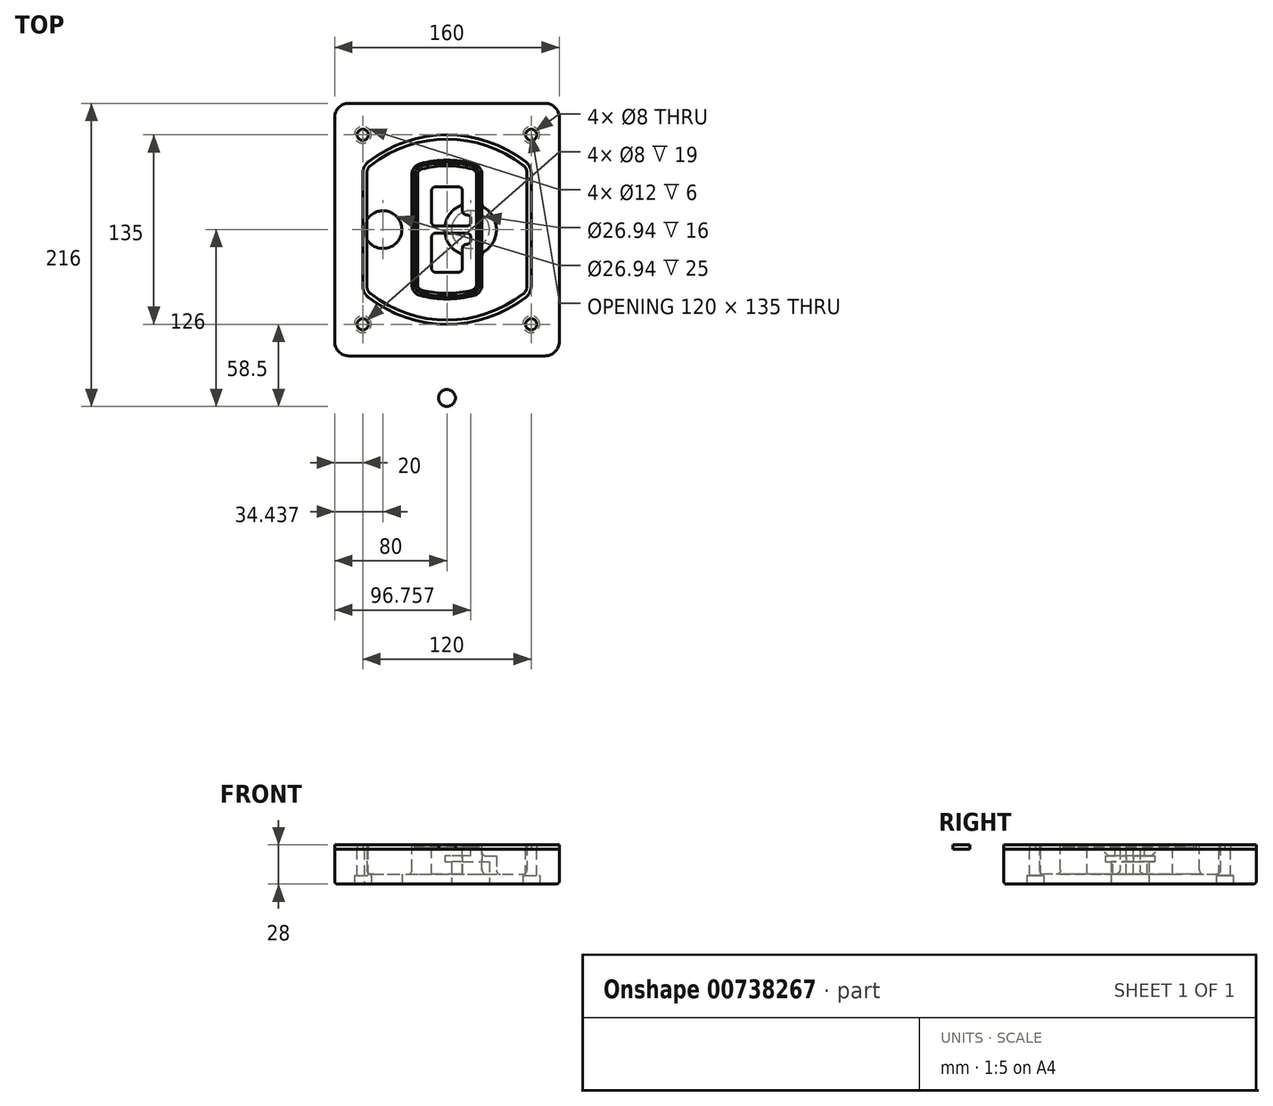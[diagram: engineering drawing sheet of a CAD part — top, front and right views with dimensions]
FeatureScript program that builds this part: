
annotation { "Feature Type Name" : "Feature", "Feature Type Description" : "" }
export const myFeature = defineFeature(function(context is Context, id is Id, definition is map)
    precondition{}
    {
        {
            var Q0;
            Q0=qCreatedBy(makeId("Top.planeOp"),FACE);
            var sketch = newSketch(context, id + "F0", { "sketchPlane" : qUnion([Q0])});
            skPoint(sketch, "E0.rect.middle", {"position": v(0, 0) * mm});
            skLineSegment(sketch, "E1.bottom", {"start": v(-70, -90) * mm, "end": v(70, -90) * mm});
            skLineSegment(sketch, "E1.top", {"start": v(-70, 90) * mm, "end": v(70, 90) * mm});
            skLineSegment(sketch, "E1.left", {"start": v(-80, -80) * mm, "end": v(-80, 80) * mm});
            skLineSegment(sketch, "E1.right", {"start": v(80, -80) * mm, "end": v(80, 80) * mm});
            skLineSegment(sketch, "E2", {"start": v(-80, 90) * mm, "end": v(80, -90) * mm, "construction": true});
            skLineSegment(sketch, "E3", {"start": v(80, 90) * mm, "end": v(-80, -90) * mm, "construction": true});
            skCircle(sketch, "E4", {"center": v(-60, 67.5) * mm, "radius": 4 * mm});
            skCircle(sketch, "E5", {"center": v(60, 67.5) * mm, "radius": 4 * mm});
            skCircle(sketch, "E6", {"center": v(60, -67.5) * mm, "radius": 4 * mm});
            skCircle(sketch, "E7", {"center": v(-60, -67.5) * mm, "radius": 4 * mm});
            skLineSegment(sketch, "E8", {"start": v(-60, 67.5) * mm, "end": v(60, 67.5) * mm, "construction": true});
            skLineSegment(sketch, "E9", {"start": v(60, 67.5) * mm, "end": v(60, -67.5) * mm, "construction": true});
            skLineSegment(sketch, "E10", {"start": v(60, -67.5) * mm, "end": v(-60, -67.5) * mm, "construction": true});
            skLineSegment(sketch, "E11", {"start": v(-60, -67.5) * mm, "end": v(-60, 67.5) * mm, "construction": true});
            skLineSegment(sketch, "E12", {"start": v(-60, 40.3) * mm, "end": v(-60, -40.3) * mm});
            skLineSegment(sketch, "E13", {"start": v(60, 40.3) * mm, "end": v(60, -40.3) * mm});
            skArc(sketch, "E14", {"start": v(56.15, 48.18) * mm, "mid": v(0, 67.5) * mm, "end": v(-56.15, 48.18) * mm});
            skArc(sketch, "E15", {"start": v(-56.15, -48.18) * mm, "mid": v(0, -67.5) * mm, "end": v(56.15, -48.18) * mm});
            skLineSegment(sketch, "E16", {"start": v(-60, 0) * mm, "end": v(60, 0) * mm, "construction": true});
            skPoint(sketch, "E17.visualSharp", {"position": v(-60, -45) * mm});
            skArc(sketch, "E17.filletArc", {"start": v(-60, -40.3) * mm, "mid": v(-58.99, -44.68) * mm, "end": v(-56.15, -48.18) * mm});
            skPoint(sketch, "E18.visualSharp", {"position": v(-60, 45) * mm});
            skArc(sketch, "E18.filletArc", {"start": v(-56.15, 48.18) * mm, "mid": v(-58.99, 44.68) * mm, "end": v(-60, 40.3) * mm});
            skPoint(sketch, "E19.visualSharp", {"position": v(60, 45) * mm});
            skArc(sketch, "E19.filletArc", {"start": v(60, 40.3) * mm, "mid": v(58.99, 44.68) * mm, "end": v(56.15, 48.18) * mm});
            skPoint(sketch, "E20.visualSharp", {"position": v(60, -45) * mm});
            skArc(sketch, "E20.filletArc", {"start": v(56.15, -48.18) * mm, "mid": v(58.99, -44.68) * mm, "end": v(60, -40.3) * mm});
            skPoint(sketch, "E21.visualSharp", {"position": v(-80, 90) * mm});
            skArc(sketch, "E21.filletArc", {"start": v(-70, 90) * mm, "mid": v(-77.07, 87.07) * mm, "end": v(-80, 80) * mm});
            skPoint(sketch, "E22.visualSharp", {"position": v(80, 90) * mm});
            skArc(sketch, "E22.filletArc", {"start": v(80, 80) * mm, "mid": v(77.07, 87.07) * mm, "end": v(70, 90) * mm});
            skPoint(sketch, "E23.visualSharp", {"position": v(80, -90) * mm});
            skArc(sketch, "E23.filletArc", {"start": v(70, -90) * mm, "mid": v(77.07, -87.07) * mm, "end": v(80, -80) * mm});
            skPoint(sketch, "E24.visualSharp", {"position": v(-80, -90) * mm});
            skArc(sketch, "E24.filletArc", {"start": v(-80, -80) * mm, "mid": v(-77.07, -87.07) * mm, "end": v(-70, -90) * mm});
            skArc(sketch, "E25.0", {"start": v(57, 40.3) * mm, "mid": v(56.3, 43.36) * mm, "end": v(54.3, 45.81) * mm});
            skLineSegment(sketch, "E25.1", {"start": v(57, 40.3) * mm, "end": v(57, -40.3) * mm});
            skArc(sketch, "E25.2", {"start": v(54.3, -45.81) * mm, "mid": v(56.3, -43.36) * mm, "end": v(57, -40.3) * mm});
            skArc(sketch, "E25.3", {"start": v(-54.3, -45.81) * mm, "mid": v(0, -64.5) * mm, "end": v(54.3, -45.81) * mm});
            skArc(sketch, "E25.4", {"start": v(-57, -40.3) * mm, "mid": v(-56.3, -43.36) * mm, "end": v(-54.3, -45.81) * mm});
            skArc(sketch, "E25.5", {"start": v(54.3, 45.81) * mm, "mid": v(0, 64.5) * mm, "end": v(-54.3, 45.81) * mm});
            skLineSegment(sketch, "E25.6", {"start": v(-57, 40.3) * mm, "end": v(-57, -40.3) * mm});
            skArc(sketch, "E25.7", {"start": v(-54.3, 45.81) * mm, "mid": v(-56.3, 43.36) * mm, "end": v(-57, 40.3) * mm});
            skArc(sketch, "E26.0", {"start": v(-58.62, 51.33) * mm, "mid": v(-62.58, 46.43) * mm, "end": v(-64, 40.3) * mm});
            skArc(sketch, "E26.1", {"start": v(58.62, 51.33) * mm, "mid": v(0, 71.5) * mm, "end": v(-58.62, 51.33) * mm});
            skArc(sketch, "E26.2", {"start": v(64, 40.3) * mm, "mid": v(62.58, 46.43) * mm, "end": v(58.62, 51.33) * mm});
            skLineSegment(sketch, "E26.3", {"start": v(64, 40.3) * mm, "end": v(64, -40.3) * mm});
            skArc(sketch, "E26.4", {"start": v(58.62, -51.33) * mm, "mid": v(62.58, -46.43) * mm, "end": v(64, -40.3) * mm});
            skLineSegment(sketch, "E26.5", {"start": v(-64, 40.3) * mm, "end": v(-64, -40.3) * mm});
            skArc(sketch, "E26.6", {"start": v(-58.62, -51.33) * mm, "mid": v(0, -71.5) * mm, "end": v(58.62, -51.33) * mm});
            skArc(sketch, "E26.7", {"start": v(-64, -40.3) * mm, "mid": v(-62.58, -46.43) * mm, "end": v(-58.62, -51.33) * mm});
            skSolve(sketch);
        }
        {
            var Q0;
            Q0=makeQuery(id+"F0.imprint","IMPRINT",FACE,{"disambiguationData":[TD([[makeQuery(id+"F0.imprint","IMPRINT",EDGE,{"derivedFrom":sQuery(id+"F0.wireOp",EDGE,"E1.bottom")}),1.0]])]});
            var Q1;
            Q1=makeQuery(id+"F0.imprint","IMPRINT",FACE,{"disambiguationData":[TD([[makeQuery(id+"F0.imprint","IMPRINT",EDGE,{"derivedFrom":sQuery(id+"F0.wireOp",EDGE,"E12")}),1.0]])]});
            var Q2;
            Q2=makeQuery(id+"F0.imprint","IMPRINT",FACE,{"disambiguationData":[TD([[makeQuery(id+"F0.imprint","IMPRINT",EDGE,{"derivedFrom":sQuery(id+"F0.wireOp",EDGE,"E25.0")}),1.0]])]});
            var Q3;
            Q3=makeQuery(id+"F0.imprint","IMPRINT",FACE,{"disambiguationData":[TD([[makeQuery(id+"F0.imprint","IMPRINT",EDGE,{"derivedFrom":sQuery(id+"F0.wireOp",EDGE,"E12")}),-1.0]])]});
            extrude(context, id + "F1", {"entities" : qUnion([Q0, Q1, Q2, Q3]), "oppositeDirection" : true, "depth" : 25 * mm});
        }
        {
            var Q0;
            Q0=makeQuery(id+"F0.imprint","IMPRINT",FACE,{"disambiguationData":[TD([[makeQuery(id+"F0.imprint","IMPRINT",EDGE,{"derivedFrom":sQuery(id+"F0.wireOp",EDGE,"E12")}),1.0]])]});
            extrude(context, id + "F2", {"entities" : qUnion([Q0]), "operationType" : NewBodyOperationType.ADD, "depth" : 3 * mm});
        }
        {
            var Q0;
            Q0=makeQuery(id+"F0.imprint","IMPRINT",FACE,{"disambiguationData":[TD([[makeQuery(id+"F0.imprint","IMPRINT",EDGE,{"derivedFrom":sQuery(id+"F0.wireOp",EDGE,"E25.0")}),1.0]])]});
            extrude(context, id + "F3", {"entities" : qUnion([Q0]), "operationType" : NewBodyOperationType.REMOVE, "oppositeDirection" : true, "depth" : 18 * mm});
        }
        {
            var Q0;
            Q0=makeQuery(id+"F2.opExtrude","CAP_FACE",FACE,{"disambiguationData":[OSD([sQuery(id+"F0.wireOp",EDGE,"E12"),sQuery(id+"F0.wireOp",EDGE,"E13"),sQuery(id+"F0.wireOp",EDGE,"E14"),sQuery(id+"F0.wireOp",EDGE,"E15"),sQuery(id+"F0.wireOp",EDGE,"E17.filletArc"),sQuery(id+"F0.wireOp",EDGE,"E18.filletArc"),sQuery(id+"F0.wireOp",EDGE,"E19.filletArc"),sQuery(id+"F0.wireOp",EDGE,"E20.filletArc"),sQuery(id+"F0.wireOp",EDGE,"E25.0"),sQuery(id+"F0.wireOp",EDGE,"E25.1"),sQuery(id+"F0.wireOp",EDGE,"E25.2"),sQuery(id+"F0.wireOp",EDGE,"E25.3"),sQuery(id+"F0.wireOp",EDGE,"E25.4"),sQuery(id+"F0.wireOp",EDGE,"E25.5"),sQuery(id+"F0.wireOp",EDGE,"E25.6"),sQuery(id+"F0.wireOp",EDGE,"E25.7")])],"isStart":false});
            var sketch = newSketch(context, id + "F4", { "sketchPlane" : qUnion([Q0])});
            skArc(sketch, "E27.0", {"start": v(-19.08, -46.97) * mm, "mid": v(0, -49.5) * mm, "end": v(19.08, -46.97) * mm});
            skArc(sketch, "E28.0", {"start": v(19.08, 46.97) * mm, "mid": v(0, 49.5) * mm, "end": v(-19.08, 46.97) * mm});
            skLineSegment(sketch, "E29", {"start": v(-25, 39.25) * mm, "end": v(-25, -39.25) * mm});
            skLineSegment(sketch, "E30", {"start": v(25, 39.25) * mm, "end": v(25, -39.25) * mm});
            skLineSegment(sketch, "E31", {"start": v(-25, 45.1) * mm, "end": v(25, 45.1) * mm, "construction": true});
            skLineSegment(sketch, "E32", {"start": v(-25, -45.1) * mm, "end": v(25, -45.1) * mm, "construction": true});
            skPoint(sketch, "E33.visualSharp", {"position": v(-25, 45.1) * mm});
            skArc(sketch, "E33.filletArc", {"start": v(-19.08, 46.97) * mm, "mid": v(-23.35, 44.11) * mm, "end": v(-25, 39.25) * mm});
            skPoint(sketch, "E34.visualSharp", {"position": v(25, 45.1) * mm});
            skArc(sketch, "E34.filletArc", {"start": v(25, 39.25) * mm, "mid": v(23.35, 44.11) * mm, "end": v(19.08, 46.97) * mm});
            skPoint(sketch, "E35.visualSharp", {"position": v(25, -45.1) * mm});
            skArc(sketch, "E35.filletArc", {"start": v(19.08, -46.97) * mm, "mid": v(23.35, -44.11) * mm, "end": v(25, -39.25) * mm});
            skPoint(sketch, "E36.visualSharp", {"position": v(-25, -45.1) * mm});
            skArc(sketch, "E36.filletArc", {"start": v(-25, -39.25) * mm, "mid": v(-23.35, -44.11) * mm, "end": v(-19.08, -46.97) * mm});
            skArc(sketch, "E37.0", {"start": v(54.3, 45.81) * mm, "mid": v(0, 64.5) * mm, "end": v(-54.3, 45.81) * mm});
            skArc(sketch, "E37.1", {"start": v(-54.3, 45.81) * mm, "mid": v(-56.3, 43.36) * mm, "end": v(-57, 40.3) * mm});
            skLineSegment(sketch, "E37.2", {"start": v(-57, 40.3) * mm, "end": v(-57, -40.3) * mm});
            skArc(sketch, "E37.3", {"start": v(-57, -40.3) * mm, "mid": v(-56.3, -43.36) * mm, "end": v(-54.3, -45.81) * mm});
            skArc(sketch, "E37.4", {"start": v(-54.3, -45.81) * mm, "mid": v(0, -64.5) * mm, "end": v(54.3, -45.81) * mm});
            skArc(sketch, "E37.5", {"start": v(54.3, -45.81) * mm, "mid": v(56.3, -43.36) * mm, "end": v(57, -40.3) * mm});
            skLineSegment(sketch, "E37.6", {"start": v(57, 40.3) * mm, "end": v(57, -40.3) * mm});
            skArc(sketch, "E37.7", {"start": v(57, 40.3) * mm, "mid": v(56.3, 43.36) * mm, "end": v(54.3, 45.81) * mm});
            skLineSegment(sketch, "E38.0", {"start": v(23, 39.25) * mm, "end": v(23, -39.25) * mm});
            skArc(sketch, "E38.1", {"start": v(18.56, -45.04) * mm, "mid": v(21.76, -42.9) * mm, "end": v(23, -39.25) * mm});
            skArc(sketch, "E38.2", {"start": v(-18.56, -45.04) * mm, "mid": v(0, -47.5) * mm, "end": v(18.56, -45.04) * mm});
            skArc(sketch, "E38.3", {"start": v(-23, -39.25) * mm, "mid": v(-21.76, -42.9) * mm, "end": v(-18.56, -45.04) * mm});
            skLineSegment(sketch, "E38.4", {"start": v(-23, 39.25) * mm, "end": v(-23, -39.25) * mm});
            skArc(sketch, "E38.5", {"start": v(23, 39.25) * mm, "mid": v(21.76, 42.9) * mm, "end": v(18.56, 45.04) * mm});
            skArc(sketch, "E38.6", {"start": v(-18.56, 45.04) * mm, "mid": v(-21.76, 42.9) * mm, "end": v(-23, 39.25) * mm});
            skArc(sketch, "E38.7", {"start": v(18.56, 45.04) * mm, "mid": v(0, 47.5) * mm, "end": v(-18.56, 45.04) * mm});
            skArc(sketch, "E39.0", {"start": v(21, 39.25) * mm, "mid": v(20.18, 41.68) * mm, "end": v(18.04, 43.1) * mm});
            skLineSegment(sketch, "E39.1", {"start": v(21, 39.25) * mm, "end": v(21, -39.25) * mm});
            skArc(sketch, "E39.2", {"start": v(18.04, -43.1) * mm, "mid": v(20.18, -41.68) * mm, "end": v(21, -39.25) * mm});
            skArc(sketch, "E39.3", {"start": v(-18.04, -43.1) * mm, "mid": v(0, -45.5) * mm, "end": v(18.04, -43.1) * mm});
            skArc(sketch, "E39.4", {"start": v(-21, -39.25) * mm, "mid": v(-20.18, -41.68) * mm, "end": v(-18.04, -43.1) * mm});
            skArc(sketch, "E39.5", {"start": v(18.04, 43.1) * mm, "mid": v(0, 45.5) * mm, "end": v(-18.04, 43.1) * mm});
            skLineSegment(sketch, "E39.6", {"start": v(-21, 39.25) * mm, "end": v(-21, -39.25) * mm});
            skArc(sketch, "E39.7", {"start": v(-18.04, 43.1) * mm, "mid": v(-20.18, 41.68) * mm, "end": v(-21, 39.25) * mm});
            skLineSegment(sketch, "E40", {"start": v(-25, 0) * mm, "end": v(25, 0) * mm, "construction": true});
            skLineSegment(sketch, "E41", {"start": v(-11, 5.5) * mm, "end": v(-11, 27.5) * mm});
            skLineSegment(sketch, "E42", {"start": v(-8, 30.5) * mm, "end": v(8, 30.5) * mm});
            skLineSegment(sketch, "E43", {"start": v(11, 27.5) * mm, "end": v(11, 13.5) * mm});
            skLineSegment(sketch, "E44", {"start": v(14, 10.5) * mm, "end": v(14, 10.5) * mm});
            skLineSegment(sketch, "E45", {"start": v(17, 7.5) * mm, "end": v(17, 5.5) * mm});
            skLineSegment(sketch, "E46", {"start": v(14, 2.5) * mm, "end": v(-8, 2.5) * mm});
            skPoint(sketch, "E47.visualSharp", {"position": v(-11, 30.5) * mm});
            skArc(sketch, "E47.filletArc", {"start": v(-8, 30.5) * mm, "mid": v(-10.12, 29.62) * mm, "end": v(-11, 27.5) * mm});
            skPoint(sketch, "E48.visualSharp", {"position": v(11, 30.5) * mm});
            skArc(sketch, "E48.filletArc", {"start": v(11, 27.5) * mm, "mid": v(10.12, 29.62) * mm, "end": v(8, 30.5) * mm});
            skPoint(sketch, "E49.visualSharp", {"position": v(11, 10.5) * mm});
            skArc(sketch, "E49.filletArc", {"start": v(11, 13.5) * mm, "mid": v(11.88, 11.38) * mm, "end": v(14, 10.5) * mm});
            skPoint(sketch, "E50.visualSharp", {"position": v(17, 10.5) * mm});
            skArc(sketch, "E50.filletArc", {"start": v(17, 7.5) * mm, "mid": v(16.12, 9.62) * mm, "end": v(14, 10.5) * mm});
            skPoint(sketch, "E51.visualSharp", {"position": v(17, 2.5) * mm});
            skArc(sketch, "E51.filletArc", {"start": v(14, 2.5) * mm, "mid": v(16.12, 3.38) * mm, "end": v(17, 5.5) * mm});
            skPoint(sketch, "E52.visualSharp", {"position": v(-11, 2.5) * mm});
            skArc(sketch, "E52.filletArc", {"start": v(-11, 5.5) * mm, "mid": v(-10.12, 3.38) * mm, "end": v(-8, 2.5) * mm});
            skLineSegment(sketch, "E53.0.MirrorCS", {"start": v(14, -2.5) * mm, "end": v(-8, -2.5) * mm});
            skArc(sketch, "E54.0.MirrorCS", {"start": v(-11, -5.5) * mm, "mid": v(-10.12, -3.38) * mm, "end": v(-8, -2.5) * mm});
            skLineSegment(sketch, "E55.0.MirrorCS", {"start": v(-11, -5.5) * mm, "end": v(-11, -27.5) * mm});
            skArc(sketch, "E56.0.MirrorCS", {"start": v(-8, -30.5) * mm, "mid": v(-10.12, -29.62) * mm, "end": v(-11, -27.5) * mm});
            skLineSegment(sketch, "E57.0.MirrorCS", {"start": v(-8, -30.5) * mm, "end": v(8, -30.5) * mm});
            skArc(sketch, "E58.0.MirrorCS", {"start": v(11, -27.5) * mm, "mid": v(10.12, -29.62) * mm, "end": v(8, -30.5) * mm});
            skLineSegment(sketch, "E59.0.MirrorCS", {"start": v(11, -27.5) * mm, "end": v(11, -13.5) * mm});
            skArc(sketch, "E60.0.MirrorCS", {"start": v(11, -13.5) * mm, "mid": v(11.88, -11.38) * mm, "end": v(14, -10.5) * mm});
            skArc(sketch, "E61.0.MirrorCS", {"start": v(17, -7.5) * mm, "mid": v(16.12, -9.62) * mm, "end": v(14, -10.5) * mm});
            skLineSegment(sketch, "E62.0.MirrorCS", {"start": v(17, -7.5) * mm, "end": v(17, -5.5) * mm});
            skArc(sketch, "E63.0.MirrorCS", {"start": v(14, -2.5) * mm, "mid": v(16.12, -3.38) * mm, "end": v(17, -5.5) * mm});
            skSolve(sketch);
        }
        {
            var Q0;
            Q0=makeQuery(id+"F4.imprint","IMPRINT",FACE,{"disambiguationData":[TD([[makeQuery(id+"F4.imprint","IMPRINT",EDGE,{"derivedFrom":sQuery(id+"F4.wireOp",EDGE,"E27.0")}),1.0]])]});
            var Q1;
            Q1=makeQuery(id+"F4.imprint","IMPRINT",FACE,{"disambiguationData":[TD([[makeQuery(id+"F4.imprint","IMPRINT",EDGE,{"derivedFrom":sQuery(id+"F4.wireOp",EDGE,"E38.0")}),-1.0]])]});
            var Q2;
            Q2=makeQuery(id+"F4.imprint","IMPRINT",FACE,{"disambiguationData":[TD([[makeQuery(id+"F4.imprint","IMPRINT",EDGE,{"derivedFrom":sQuery(id+"F4.wireOp",EDGE,"E39.0")}),1.0]])]});
            extrude(context, id + "F5", {"entities" : qUnion([Q0, Q1, Q2]), "operationType" : NewBodyOperationType.ADD, "endBound" : BoundingType.UP_TO_NEXT, "oppositeDirection" : true, "depth" : 25 * mm});
        }
        {
            var Q0;
            Q0=makeQuery(id+"F4.imprint","IMPRINT",FACE,{"disambiguationData":[TD([[makeQuery(id+"F4.imprint","IMPRINT",EDGE,{"derivedFrom":sQuery(id+"F4.wireOp",EDGE,"E38.0")}),-1.0]])]});
            extrude(context, id + "F6", {"entities" : qUnion([Q0]), "operationType" : NewBodyOperationType.REMOVE, "oppositeDirection" : true, "depth" : 2 * mm});
        }
        {
            var Q0;
            Q0=makeQuery(id+"F1.opExtrude","CAP_FACE",FACE,{"disambiguationData":[OSD([sQuery(id+"F0.wireOp",EDGE,"E1.bottom"),sQuery(id+"F0.wireOp",EDGE,"E1.top"),sQuery(id+"F0.wireOp",EDGE,"E1.left"),sQuery(id+"F0.wireOp",EDGE,"E1.right"),sQuery(id+"F0.wireOp",EDGE,"E4"),sQuery(id+"F0.wireOp",EDGE,"E5"),sQuery(id+"F0.wireOp",EDGE,"E6"),sQuery(id+"F0.wireOp",EDGE,"E7"),sQuery(id+"F0.wireOp",EDGE,"E21.filletArc"),sQuery(id+"F0.wireOp",EDGE,"E22.filletArc"),sQuery(id+"F0.wireOp",EDGE,"E23.filletArc"),sQuery(id+"F0.wireOp",EDGE,"E24.filletArc")])],"isStart":false});
            var sketch = newSketch(context, id + "F7", { "sketchPlane" : qUnion([Q0])});
            skCircle(sketch, "E64", {"center": v(16.76, 0) * mm, "radius": 13.47 * mm});
            skCircle(sketch, "E65", {"center": v(-45.56, 0) * mm, "radius": 13.47 * mm});
            skLineSegment(sketch, "E66", {"start": v(80, 0) * mm, "end": v(-80, 0) * mm});
            skCircle(sketch, "E67", {"center": v(16.76, 0) * mm, "radius": 18.47 * mm});
            skCircle(sketch, "E68", {"center": v(60, -67.5) * mm, "radius": 6 * mm});
            skCircle(sketch, "E69", {"center": v(-60, -67.5) * mm, "radius": 6 * mm});
            skCircle(sketch, "E70", {"center": v(-60, 67.5) * mm, "radius": 6 * mm});
            skCircle(sketch, "E71", {"center": v(60, 67.5) * mm, "radius": 6 * mm});
            skSolve(sketch);
        }
        {
            var Q0;
            {var subQ1=sQuery(id+"F7.wireOp",EDGE,"E66");var subQ4=sQuery(id+"F7.wireOp",EDGE,"E64");var subQ6=makeQuery(id+"F7.imprint","INTERSECT",VERTEX,{"disambiguationData":[OD(0.0)],"derivedFrom":[subQ4,subQ1]});Q0=makeQuery(id+"F7.imprint","IMPRINT",FACE,{"disambiguationData":[TD([[makeQuery(id+"F7.imprint","IMPRINT",EDGE,{"disambiguationData":[TD([[subQ6,-1.0]])],"derivedFrom":subQ4}),-1.0]])]});}
            var Q1;
            {var subQ0=sQuery(id+"F7.wireOp",EDGE,"E66");var subQ1=sQuery(id+"F7.wireOp",EDGE,"E64");var subQ3=makeQuery(id+"F7.imprint","INTERSECT",VERTEX,{"disambiguationData":[OD(0.0)],"derivedFrom":[subQ1,subQ0]});Q1=makeQuery(id+"F7.imprint","IMPRINT",FACE,{"disambiguationData":[TD([[makeQuery(id+"F7.imprint","IMPRINT",EDGE,{"disambiguationData":[TD([[subQ3,-1.0]])],"derivedFrom":subQ1}),1.0]])]});}
            var Q2;
            {var subQ0=sQuery(id+"F7.wireOp",EDGE,"E66");var subQ1=sQuery(id+"F7.wireOp",EDGE,"E64");var subQ3=makeQuery(id+"F7.imprint","INTERSECT",VERTEX,{"disambiguationData":[OD(0.0)],"derivedFrom":[subQ1,subQ0]});Q2=makeQuery(id+"F7.imprint","IMPRINT",FACE,{"disambiguationData":[TD([[makeQuery(id+"F7.imprint","IMPRINT",EDGE,{"disambiguationData":[TD([[subQ3,1.0]])],"derivedFrom":subQ1}),1.0]])]});}
            var Q3;
            {var subQ1=sQuery(id+"F7.wireOp",EDGE,"E66");var subQ4=sQuery(id+"F7.wireOp",EDGE,"E64");var subQ6=makeQuery(id+"F7.imprint","INTERSECT",VERTEX,{"disambiguationData":[OD(0.0)],"derivedFrom":[subQ4,subQ1]});Q3=makeQuery(id+"F7.imprint","IMPRINT",FACE,{"disambiguationData":[TD([[makeQuery(id+"F7.imprint","IMPRINT",EDGE,{"disambiguationData":[TD([[subQ6,1.0]])],"derivedFrom":subQ4}),-1.0]])]});}
            extrude(context, id + "F8", {"entities" : qUnion([Q0, Q1, Q2, Q3]), "operationType" : NewBodyOperationType.ADD, "oppositeDirection" : true, "depth" : 20 * mm});
        }
        {
            var Q0;
            {var subQ0=sQuery(id+"F7.wireOp",EDGE,"E66");var subQ1=sQuery(id+"F7.wireOp",EDGE,"E64");var subQ3=makeQuery(id+"F7.imprint","INTERSECT",VERTEX,{"disambiguationData":[OD(0.0)],"derivedFrom":[subQ1,subQ0]});Q0=makeQuery(id+"F7.imprint","IMPRINT",FACE,{"disambiguationData":[TD([[makeQuery(id+"F7.imprint","IMPRINT",EDGE,{"disambiguationData":[TD([[subQ3,-1.0]])],"derivedFrom":subQ1}),1.0]])]});}
            var Q1;
            {var subQ0=sQuery(id+"F7.wireOp",EDGE,"E66");var subQ1=sQuery(id+"F7.wireOp",EDGE,"E64");var subQ3=makeQuery(id+"F7.imprint","INTERSECT",VERTEX,{"disambiguationData":[OD(0.0)],"derivedFrom":[subQ1,subQ0]});Q1=makeQuery(id+"F7.imprint","IMPRINT",FACE,{"disambiguationData":[TD([[makeQuery(id+"F7.imprint","IMPRINT",EDGE,{"disambiguationData":[TD([[subQ3,1.0]])],"derivedFrom":subQ1}),1.0]])]});}
            extrude(context, id + "F9", {"entities" : qUnion([Q0, Q1]), "operationType" : NewBodyOperationType.REMOVE, "oppositeDirection" : true, "depth" : 16 * mm});
        }
        {
            var Q0;
            {var subQ0=sQuery(id+"F7.wireOp",EDGE,"E66");var subQ1=sQuery(id+"F7.wireOp",EDGE,"E65");var subQ3=makeQuery(id+"F7.imprint","INTERSECT",VERTEX,{"disambiguationData":[OD(0.0)],"derivedFrom":[subQ1,subQ0]});Q0=makeQuery(id+"F7.imprint","IMPRINT",FACE,{"disambiguationData":[TD([[makeQuery(id+"F7.imprint","IMPRINT",EDGE,{"disambiguationData":[TD([[subQ3,-1.0]])],"derivedFrom":subQ1}),1.0]])]});}
            var Q1;
            {var subQ0=sQuery(id+"F7.wireOp",EDGE,"E66");var subQ1=sQuery(id+"F7.wireOp",EDGE,"E65");var subQ3=makeQuery(id+"F7.imprint","INTERSECT",VERTEX,{"disambiguationData":[OD(0.0)],"derivedFrom":[subQ1,subQ0]});Q1=makeQuery(id+"F7.imprint","IMPRINT",FACE,{"disambiguationData":[TD([[makeQuery(id+"F7.imprint","IMPRINT",EDGE,{"disambiguationData":[TD([[subQ3,1.0]])],"derivedFrom":subQ1}),1.0]])]});}
            extrude(context, id + "F10", {"entities" : qUnion([Q0, Q1]), "operationType" : NewBodyOperationType.REMOVE, "oppositeDirection" : true, "depth" : 25 * mm});
        }
        {
            var Q0;
            Q0=makeQuery(id+"F7.imprint","IMPRINT",FACE,{"disambiguationData":[TD([[makeQuery(id+"F7.imprint","IMPRINT",EDGE,{"derivedFrom":sQuery(id+"F7.wireOp",EDGE,"E68")}),1.0]])]});
            var Q1;
            Q1=makeQuery(id+"F7.imprint","IMPRINT",FACE,{"disambiguationData":[TD([[makeQuery(id+"F7.imprint","IMPRINT",EDGE,{"derivedFrom":makeQuery(id+"F1.opExtrude","CAP_EDGE",EDGE,{"disambiguationData":[OSD([sQuery(id+"F0.wireOp",EDGE,"E5")])],"isStart":false})}),-1.0]])]});
            var Q2;
            Q2=makeQuery(id+"F7.imprint","IMPRINT",FACE,{"disambiguationData":[TD([[makeQuery(id+"F7.imprint","IMPRINT",EDGE,{"derivedFrom":sQuery(id+"F7.wireOp",EDGE,"E69")}),1.0]])]});
            var Q3;
            Q3=makeQuery(id+"F7.imprint","IMPRINT",FACE,{"disambiguationData":[TD([[makeQuery(id+"F7.imprint","IMPRINT",EDGE,{"derivedFrom":makeQuery(id+"F1.opExtrude","CAP_EDGE",EDGE,{"disambiguationData":[OSD([sQuery(id+"F0.wireOp",EDGE,"E4")])],"isStart":false})}),-1.0]])]});
            var Q4;
            Q4=makeQuery(id+"F7.imprint","IMPRINT",FACE,{"disambiguationData":[TD([[makeQuery(id+"F7.imprint","IMPRINT",EDGE,{"derivedFrom":sQuery(id+"F7.wireOp",EDGE,"E70")}),1.0]])]});
            var Q5;
            Q5=makeQuery(id+"F7.imprint","IMPRINT",FACE,{"disambiguationData":[TD([[makeQuery(id+"F7.imprint","IMPRINT",EDGE,{"derivedFrom":makeQuery(id+"F1.opExtrude","CAP_EDGE",EDGE,{"disambiguationData":[OSD([sQuery(id+"F0.wireOp",EDGE,"E7")])],"isStart":false})}),-1.0]])]});
            var Q6;
            Q6=makeQuery(id+"F7.imprint","IMPRINT",FACE,{"disambiguationData":[TD([[makeQuery(id+"F7.imprint","IMPRINT",EDGE,{"derivedFrom":sQuery(id+"F7.wireOp",EDGE,"E71")}),1.0]])]});
            var Q7;
            Q7=makeQuery(id+"F7.imprint","IMPRINT",FACE,{"disambiguationData":[TD([[makeQuery(id+"F7.imprint","IMPRINT",EDGE,{"derivedFrom":makeQuery(id+"F1.opExtrude","CAP_EDGE",EDGE,{"disambiguationData":[OSD([sQuery(id+"F0.wireOp",EDGE,"E6")])],"isStart":false})}),-1.0]])]});
            extrude(context, id + "F11", {"entities" : qUnion([Q0, Q1, Q2, Q3, Q4, Q5, Q6, Q7]), "operationType" : NewBodyOperationType.REMOVE, "oppositeDirection" : true, "depth" : 6 * mm});
        }
        {
            var Q0;
            Q0=makeQuery(id+"F9.boolean.opBoolean","COPY",FACE,{"derivedFrom":makeQuery(id+"F9.opExtrude","CAP_FACE",FACE,{"disambiguationData":[OSD([sQuery(id+"F7.wireOp",EDGE,"E64")])],"isStart":false})});
            var sketch = newSketch(context, id + "F12", { "sketchPlane" : qUnion([Q0])});
            skArc(sketch, "E72.0", {"start": v(11, 17.55) * mm, "mid": v(2.57, 11.82) * mm, "end": v(-1.54, 2.5) * mm});
            skArc(sketch, "E72.1", {"start": v(-1.54, -2.5) * mm, "mid": v(2.57, -11.82) * mm, "end": v(11, -17.55) * mm});
            skLineSegment(sketch, "E73", {"start": v(-1.54, -2.5) * mm, "end": v(14, -2.5) * mm});
            skLineSegment(sketch, "E74.0", {"start": v(14, 2.5) * mm, "end": v(-1.54, 2.5) * mm});
            skArc(sketch, "E74.1", {"start": v(14, 2.5) * mm, "mid": v(16.12, 3.38) * mm, "end": v(17, 5.5) * mm});
            skLineSegment(sketch, "E74.2", {"start": v(17, 7.5) * mm, "end": v(17, 5.5) * mm});
            skArc(sketch, "E74.3", {"start": v(17, 7.5) * mm, "mid": v(16.12, 9.62) * mm, "end": v(14, 10.5) * mm});
            skArc(sketch, "E74.4", {"start": v(11, 13.5) * mm, "mid": v(11.88, 11.38) * mm, "end": v(14, 10.5) * mm});
            skLineSegment(sketch, "E74.5", {"start": v(11, 17.55) * mm, "end": v(11, 13.5) * mm});
            skLineSegment(sketch, "E74.7", {"start": v(14, -2.5) * mm, "end": v(-1.54, -2.5) * mm});
            skArc(sketch, "E74.8", {"start": v(14, -2.5) * mm, "mid": v(16.12, -3.38) * mm, "end": v(17, -5.5) * mm});
            skLineSegment(sketch, "E74.9", {"start": v(17, -7.5) * mm, "end": v(17, -5.5) * mm});
            skArc(sketch, "E74.10", {"start": v(17, -7.5) * mm, "mid": v(16.12, -9.62) * mm, "end": v(14, -10.5) * mm});
            skArc(sketch, "E74.11", {"start": v(11, -13.5) * mm, "mid": v(11.88, -11.38) * mm, "end": v(14, -10.5) * mm});
            skLineSegment(sketch, "E74.12", {"start": v(11, -17.55) * mm, "end": v(11, -13.5) * mm});
            skPoint(sketch, "E75.orphan", {"position": v(11, -27.5) * mm});
            skPoint(sketch, "E76.orphan", {"position": v(-8, -2.5) * mm});
            skPoint(sketch, "E77.orphan", {"position": v(-8, 2.5) * mm});
            skPoint(sketch, "E78.orphan", {"position": v(11, 27.5) * mm});
            skSolve(sketch);
        }
        {
            var Q0;
            {var subQ7=sQuery(id+"F12.wireOp",EDGE,"E72.0");var subQ14=sQuery(id+"F12.wireOp",EDGE,"E72.1");var subQ16=sQuery(id+"F12.wireOp",EDGE,"E74.1");var subQ18=sQuery(id+"F12.wireOp",EDGE,"E74.8");Q0=qUnion([makeQuery(id+"F12.imprint","IMPRINT",FACE,{"disambiguationData":[TD([[makeQuery(id+"F12.imprint","IMPRINT",EDGE,{"derivedFrom":subQ7}),1.0]])]}),makeQuery(id+"F12.imprint","IMPRINT",FACE,{"disambiguationData":[TD([[makeQuery(id+"F12.imprint","IMPRINT",EDGE,{"derivedFrom":subQ14}),1.0]])]}),makeQuery(id+"F12.imprint","IMPRINT",FACE,{"disambiguationData":[TD([[makeQuery(id+"F12.imprint","IMPRINT",EDGE,{"derivedFrom":subQ16}),1.0]])]}),makeQuery(id+"F12.imprint","IMPRINT",FACE,{"disambiguationData":[TD([[makeQuery(id+"F12.imprint","IMPRINT",EDGE,{"derivedFrom":subQ18}),-1.0]])]})]);}
            var Q1;
            Q1=makeQuery(id+"F5.boolean.opBoolean","SPLIT",FACE,{"disambiguationData":[TD([makeQuery(id+"F5.opExtrude","SWEPT_FACE",FACE,{"disambiguationData":[OSD([sQuery(id+"F4.wireOp",EDGE,"E41")])]})])],"derivedFrom":makeQuery(id+"F3.boolean.opBoolean","COPY",FACE,{"derivedFrom":makeQuery(id+"F3.opExtrude","CAP_FACE",FACE,{"disambiguationData":[OSD([sQuery(id+"F0.wireOp",EDGE,"E25.0"),sQuery(id+"F0.wireOp",EDGE,"E25.1"),sQuery(id+"F0.wireOp",EDGE,"E25.2"),sQuery(id+"F0.wireOp",EDGE,"E25.3"),sQuery(id+"F0.wireOp",EDGE,"E25.4"),sQuery(id+"F0.wireOp",EDGE,"E25.5"),sQuery(id+"F0.wireOp",EDGE,"E25.6"),sQuery(id+"F0.wireOp",EDGE,"E25.7")])],"isStart":false})})});
            extrude(context, id + "F13", {"entities" : qUnion([Q0]), "operationType" : NewBodyOperationType.REMOVE, "endBound" : BoundingType.UP_TO_SURFACE, "endBoundEntityFace" : qUnion([Q1]), "depth" : 25 * mm});
        }
        {
            var Q0;
            Q0=makeQuery(id+"F3.boolean.opBoolean","COPY",EDGE,{"derivedFrom":makeQuery(id+"F3.opExtrude","CAP_EDGE",EDGE,{"disambiguationData":[OSD([sQuery(id+"F0.wireOp",EDGE,"E25.6")])],"isStart":false})});
            var Q1;
            Q1=makeQuery(id+"F8.boolean.opBoolean","INTERSECT",EDGE,{"derivedFrom":[makeQuery(id+"F5.opExtrude","SWEPT_FACE",FACE,{"disambiguationData":[OSD([sQuery(id+"F4.wireOp",EDGE,"E30")])]}),makeQuery(id+"F8.opExtrude","CAP_FACE",FACE,{"disambiguationData":[OSD([sQuery(id+"F7.wireOp",EDGE,"E67")])],"isStart":false})]});
            var Q2;
            Q2=makeQuery(id+"F8.boolean.opBoolean","INTERSECT",EDGE,{"disambiguationData":[OD(1.0)],"derivedFrom":[makeQuery(id+"F5.opExtrude","SWEPT_FACE",FACE,{"disambiguationData":[OSD([sQuery(id+"F4.wireOp",EDGE,"E30")])]}),makeQuery(id+"F8.opExtrude","SWEPT_FACE",FACE,{"disambiguationData":[OSD([sQuery(id+"F7.wireOp",EDGE,"E67")])]})]});
            var Q3;
            {var subQ0=sQuery(id+"F4.wireOp",EDGE,"E30");Q3=makeQuery(id+"F8.boolean.opBoolean","SPLIT",EDGE,{"disambiguationData":[TD([makeQuery(id+"F5.opExtrude","SWEPT_FACE",FACE,{"disambiguationData":[OSD([sQuery(id+"F4.wireOp",EDGE,"E35.filletArc")])]})])],"derivedFrom":makeQuery(id+"F5.opExtrude","CAP_EDGE",EDGE,{"disambiguationData":[OSD([subQ0])],"isStart":false})});}
            var Q4;
            {var subQ0=sQuery(id+"F0.wireOp",EDGE,"E25.7");var subQ1=sQuery(id+"F0.wireOp",EDGE,"E25.1");var subQ2=sQuery(id+"F0.wireOp",EDGE,"E25.6");var subQ3=sQuery(id+"F0.wireOp",EDGE,"E25.5");var subQ4=sQuery(id+"F0.wireOp",EDGE,"E25.4");var subQ5=sQuery(id+"F0.wireOp",EDGE,"E25.0");var subQ6=sQuery(id+"F0.wireOp",EDGE,"E25.2");var subQ7=sQuery(id+"F0.wireOp",EDGE,"E25.3");Q4=makeQuery(id+"F8.boolean.opBoolean","INTERSECT",EDGE,{"derivedFrom":[makeQuery(id+"F5.boolean.opBoolean","SPLIT",FACE,{"disambiguationData":[TD([makeQuery(id+"F2.opExtrude","SWEPT_FACE",FACE,{"disambiguationData":[OSD([subQ5])]})])],"derivedFrom":makeQuery(id+"F3.boolean.opBoolean","COPY",FACE,{"derivedFrom":makeQuery(id+"F3.opExtrude","CAP_FACE",FACE,{"disambiguationData":[OSD([subQ5,subQ1,subQ6,subQ7,subQ4,subQ3,subQ2,subQ0])],"isStart":false})})}),makeQuery(id+"F8.opExtrude","SWEPT_FACE",FACE,{"disambiguationData":[OSD([sQuery(id+"F7.wireOp",EDGE,"E67")])]})]});}
            var Q5;
            Q5=makeQuery(id+"F8.boolean.opBoolean","INTERSECT",EDGE,{"disambiguationData":[OD(0.0)],"derivedFrom":[makeQuery(id+"F5.opExtrude","SWEPT_FACE",FACE,{"disambiguationData":[OSD([sQuery(id+"F4.wireOp",EDGE,"E30")])]}),makeQuery(id+"F8.opExtrude","SWEPT_FACE",FACE,{"disambiguationData":[OSD([sQuery(id+"F7.wireOp",EDGE,"E67")])]})]});
            fillet(context, id + "F14", {"entities" : qUnion([Q0, Q1, Q2, Q3, Q4, Q5]), "radius" : 3 * mm, "tangentPropagation" : true, "allowEdgeOverflow" : false});
        }
        {
            var Q0;
            Q0=makeQuery(id+"F1.opExtrude","CAP_EDGE",EDGE,{"disambiguationData":[OSD([sQuery(id+"F0.wireOp",EDGE,"E1.bottom")])],"isStart":false});
            fillet(context, id + "F15", {"entities" : qUnion([Q0]), "radius" : 2 * mm, "tangentPropagation" : true, "allowEdgeOverflow" : false});
        }
        {
            var Q0;
            {var subQ0=sQuery(id+"F0.wireOp",EDGE,"E21.filletArc");var subQ1=sQuery(id+"F0.wireOp",EDGE,"E7");var subQ2=sQuery(id+"F0.wireOp",EDGE,"E6");var subQ3=sQuery(id+"F0.wireOp",EDGE,"E5");var subQ4=sQuery(id+"F0.wireOp",EDGE,"E4");var subQ5=sQuery(id+"F0.wireOp",EDGE,"E22.filletArc");var subQ6=sQuery(id+"F0.wireOp",EDGE,"E1.bottom");var subQ7=sQuery(id+"F0.wireOp",EDGE,"E1.right");var subQ8=sQuery(id+"F0.wireOp",EDGE,"E1.top");var subQ9=sQuery(id+"F0.wireOp",EDGE,"E1.left");var subQ10=sQuery(id+"F0.wireOp",EDGE,"E23.filletArc");var subQ11=sQuery(id+"F0.wireOp",EDGE,"E24.filletArc");Q0=makeQuery(id+"F2.boolean.opBoolean","SPLIT",FACE,{"disambiguationData":[TD([makeQuery(id+"F1.opExtrude","SWEPT_FACE",FACE,{"disambiguationData":[OSD([subQ6])]})])],"derivedFrom":makeQuery(id+"F1.opExtrude","CAP_FACE",FACE,{"disambiguationData":[OSD([subQ6,subQ8,subQ9,subQ7,subQ4,subQ3,subQ2,subQ1,subQ0,subQ5,subQ10,subQ11])],"isStart":true})});}
            var sketch = newSketch(context, id + "F16", { "sketchPlane" : qUnion([Q0])});
            skPoint(sketch, "E79", {"position": v(0, 90) * mm});
            skLineSegment(sketch, "E80.0", {"start": v(-70, 90) * mm, "end": v(70, 90) * mm});
            skLineSegment(sketch, "E80.1", {"start": v(80, -80) * mm, "end": v(80, 80) * mm});
            skCircle(sketch, "E80.2", {"center": v(60, 67.5) * mm, "radius": 4 * mm});
            skLineSegment(sketch, "E80.3", {"start": v(-70, -90) * mm, "end": v(70, -90) * mm});
            skCircle(sketch, "E80.4", {"center": v(60, -67.5) * mm, "radius": 4 * mm});
            skCircle(sketch, "E80.5", {"center": v(-60, -67.5) * mm, "radius": 4 * mm});
            skLineSegment(sketch, "E80.6", {"start": v(-80, -80) * mm, "end": v(-80, 80) * mm});
            skCircle(sketch, "E80.7", {"center": v(-60, 67.5) * mm, "radius": 4 * mm});
            skArc(sketch, "E80.8", {"start": v(56.15, 48.18) * mm, "mid": v(0, 67.5) * mm, "end": v(-56.15, 48.18) * mm});
            skLineSegment(sketch, "E80.9", {"start": v(60, 40.3) * mm, "end": v(60, -40.3) * mm});
            skArc(sketch, "E80.10", {"start": v(-56.15, -48.18) * mm, "mid": v(0, -67.5) * mm, "end": v(56.15, -48.18) * mm});
            skLineSegment(sketch, "E80.11", {"start": v(-60, 40.3) * mm, "end": v(-60, -40.3) * mm});
            skArc(sketch, "E80.12", {"start": v(60, 40.3) * mm, "mid": v(58.99, 44.68) * mm, "end": v(56.15, 48.18) * mm});
            skArc(sketch, "E80.13", {"start": v(-56.15, 48.18) * mm, "mid": v(-58.99, 44.68) * mm, "end": v(-60, 40.3) * mm});
            skArc(sketch, "E80.14", {"start": v(56.15, -48.18) * mm, "mid": v(58.99, -44.68) * mm, "end": v(60, -40.3) * mm});
            skArc(sketch, "E80.15", {"start": v(-60, -40.3) * mm, "mid": v(-58.99, -44.68) * mm, "end": v(-56.15, -48.18) * mm});
            skArc(sketch, "E80.16", {"start": v(70, -90) * mm, "mid": v(77.07, -87.07) * mm, "end": v(80, -80) * mm});
            skArc(sketch, "E80.17", {"start": v(80, 80) * mm, "mid": v(77.07, 87.07) * mm, "end": v(70, 90) * mm});
            skArc(sketch, "E80.18", {"start": v(-80, -80) * mm, "mid": v(-77.07, -87.07) * mm, "end": v(-70, -90) * mm});
            skArc(sketch, "E80.19", {"start": v(-70, 90) * mm, "mid": v(-77.07, 87.07) * mm, "end": v(-80, 80) * mm});
            skLineSegment(sketch, "E81", {"start": v(0, 90) * mm, "end": v(0, 120) * mm, "construction": true});
            skCircle(sketch, "E82", {"center": v(0, 120) * mm, "radius": 6 * mm});
            skLineSegment(sketch, "E83", {"start": v(-15, 120) * mm, "end": v(-15, 108) * mm});
            skLineSegment(sketch, "E84", {"start": v(-15, 108) * mm, "end": v(-33, 90) * mm});
            skLineSegment(sketch, "E85", {"start": v(15, 120) * mm, "end": v(15, 108) * mm});
            skLineSegment(sketch, "E86", {"start": v(15, 108) * mm, "end": v(33, 90) * mm});
            skArc(sketch, "E87", {"start": v(15, 120) * mm, "mid": v(0, 135) * mm, "end": v(-15, 120) * mm});
            skLineSegment(sketch, "E88", {"start": v(-80, 0) * mm, "end": v(80, 0) * mm, "construction": true});
            skArc(sketch, "E89.MirrorCS", {"start": v(-15, 120) * mm, "mid": v(0, 135) * mm, "end": v(15, 120) * mm});
            skLineSegment(sketch, "E90.MirrorCS", {"start": v(15, -120) * mm, "end": v(15, -108) * mm});
            skCircle(sketch, "E91.MirrorC", {"center": v(0, -120) * mm, "radius": 6 * mm});
            skArc(sketch, "E92.MirrorCS", {"start": v(-15, -120) * mm, "mid": v(0, -135) * mm, "end": v(15, -120) * mm});
            skLineSegment(sketch, "E93.MirrorCS", {"start": v(-15, -120) * mm, "end": v(-15, -108) * mm});
            skArc(sketch, "E94.MirrorCS", {"start": v(15, -120) * mm, "mid": v(0, -135) * mm, "end": v(-15, -120) * mm});
            skLineSegment(sketch, "E95.MirrorCS", {"start": v(-15, -108) * mm, "end": v(-33, -90) * mm});
            skLineSegment(sketch, "E96.MirrorCS", {"start": v(15, -108) * mm, "end": v(33, -90) * mm});
            skPoint(sketch, "E97.MirrorP", {"position": v(0, -90) * mm});
            skLineSegment(sketch, "E98.MirrorCS", {"start": v(0, -90) * mm, "end": v(0, -120) * mm, "construction": true});
            skSolve(sketch);
        }
        {
            var Q0;
            Q0=makeQuery(id+"F16.imprint","IMPRINT",FACE,{"disambiguationData":[TD([[makeQuery(id+"F16.imprint","IMPRINT",EDGE,{"derivedFrom":sQuery(id+"F16.wireOp",EDGE,"E89.MirrorCS")}),-1.0]])]});
            var Q1;
            Q1=makeQuery(id+"F16.imprint","IMPRINT",FACE,{"disambiguationData":[TD([[makeQuery(id+"F16.imprint","IMPRINT",EDGE,{"derivedFrom":sQuery(id+"F16.wireOp",EDGE,"E80.1")}),1.0]])]});
            var Q2;
            Q2=makeQuery(id+"F16.imprint","IMPRINT",FACE,{"disambiguationData":[TD([[makeQuery(id+"F16.imprint","IMPRINT",EDGE,{"derivedFrom":sQuery(id+"F16.wireOp",EDGE,"E91.MirrorC")}),1.0]])]});
            var Q3;
            Q3=makeQuery(id+"F2.opExtrude","CAP_FACE",FACE,{"disambiguationData":[OSD([sQuery(id+"F0.wireOp",EDGE,"E12"),sQuery(id+"F0.wireOp",EDGE,"E13"),sQuery(id+"F0.wireOp",EDGE,"E14"),sQuery(id+"F0.wireOp",EDGE,"E15"),sQuery(id+"F0.wireOp",EDGE,"E17.filletArc"),sQuery(id+"F0.wireOp",EDGE,"E18.filletArc"),sQuery(id+"F0.wireOp",EDGE,"E19.filletArc"),sQuery(id+"F0.wireOp",EDGE,"E20.filletArc"),sQuery(id+"F0.wireOp",EDGE,"E25.0"),sQuery(id+"F0.wireOp",EDGE,"E25.1"),sQuery(id+"F0.wireOp",EDGE,"E25.2"),sQuery(id+"F0.wireOp",EDGE,"E25.3"),sQuery(id+"F0.wireOp",EDGE,"E25.4"),sQuery(id+"F0.wireOp",EDGE,"E25.5"),sQuery(id+"F0.wireOp",EDGE,"E25.6"),sQuery(id+"F0.wireOp",EDGE,"E25.7")])],"isStart":false});
            extrude(context, id + "F17", {"entities" : qUnion([Q0, Q1, Q2]), "endBound" : BoundingType.UP_TO_SURFACE, "depth" : 25 * mm, "endBoundEntityFace" : qUnion([Q3]), "offsetDistance" : 25 * mm});
        }
    });
